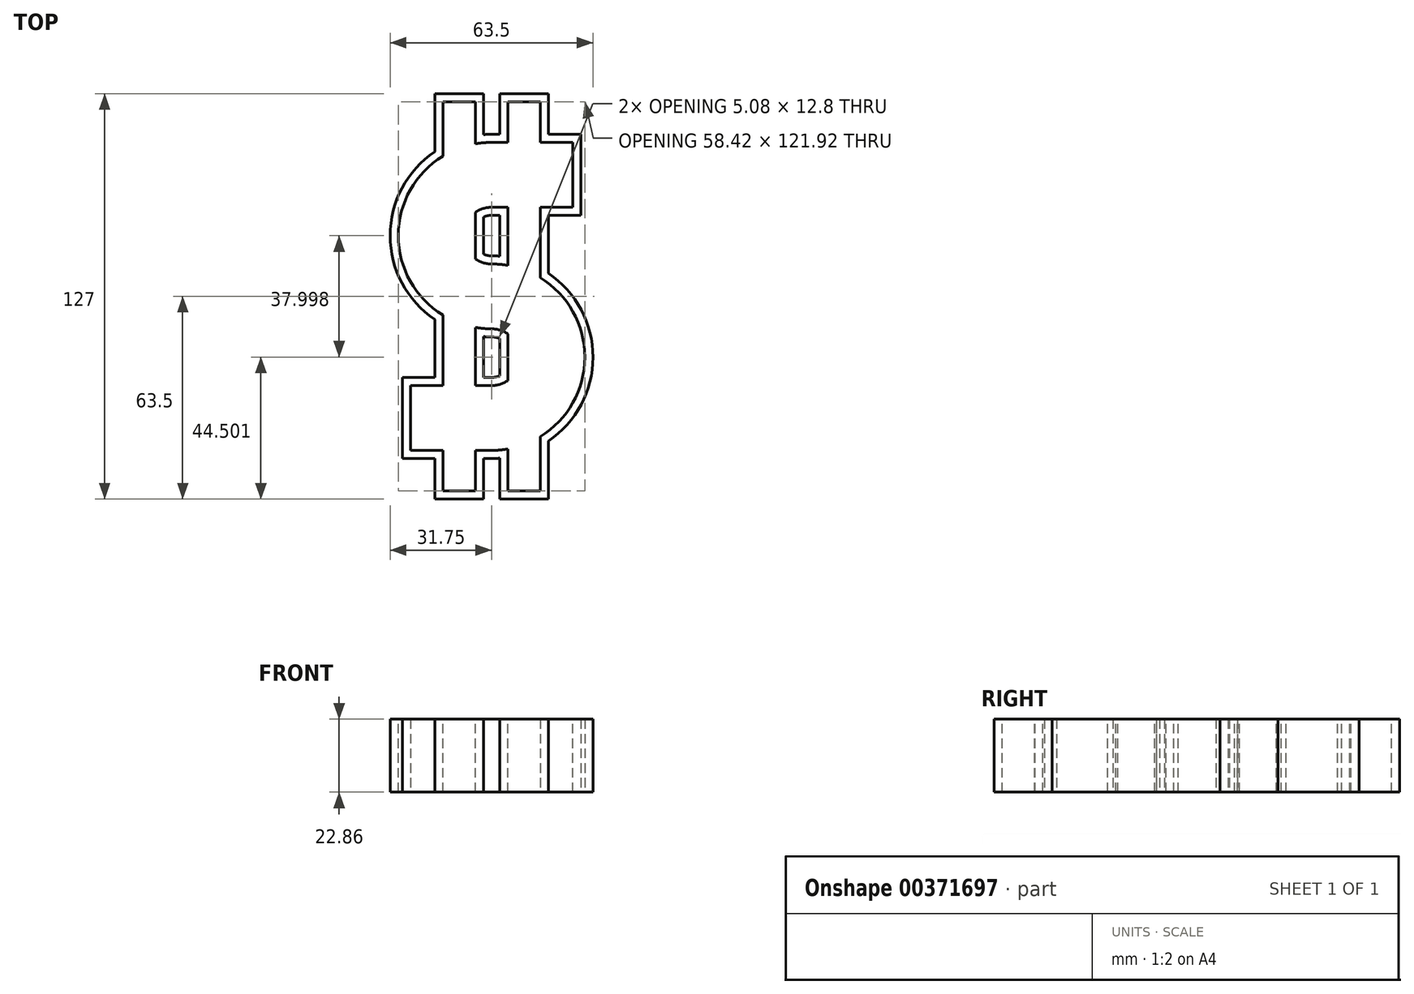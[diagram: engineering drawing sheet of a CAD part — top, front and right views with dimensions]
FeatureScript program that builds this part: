
annotation { "Feature Type Name" : "Feature", "Feature Type Description" : "" }
export const myFeature = defineFeature(function(context is Context, id is Id, definition is map)
    precondition{}
    {
        {
            var Q0;
            Q0=qCreatedBy(makeId("Top.planeOp"),FACE);
            var sketch = newSketch(context, id + "F0", { "sketchPlane" : qUnion([Q0])});
            skArc(sketch, "E0", {"start": v(0, 38.1) * mm, "mid": v(-19.05, 19.05) * mm, "end": v(0, 0) * mm});
            skArc(sketch, "E1", {"start": v(0, -38.1) * mm, "mid": v(19.05, -19.05) * mm, "end": v(0, 0) * mm});
            skLineSegment(sketch, "E2", {"start": v(-75.44, 0) * mm, "end": v(75.44, 0) * mm, "construction": true});
            skPoint(sketch, "E3", {"position": v(0, 38.1) * mm});
            skPoint(sketch, "E4", {"position": v(0, -38.1) * mm});
            skLineSegment(sketch, "E5", {"start": v(0, 38.1) * mm, "end": v(27.94, 38.1) * mm});
            skLineSegment(sketch, "E6", {"start": v(0, -38.1) * mm, "end": v(-27.94, -38.1) * mm});
            skSolve(sketch);
        }
        {
            var Q0;
            Q0=qCreatedBy(makeId("Right.planeOp"),FACE);
            cPlane(context, id + "F1", {"entities" : qUnion([Q0]), "cplaneType" : CPlaneType.OFFSET, "offset" : 27.94 * mm, "width" : 152.4 * mm, "height" : 152.4 * mm});
        }
        {
            var Q0;
            Q0=qCreatedBy(id+"F1.planeOp",FACE);
            var sketch = newSketch(context, id + "F2", { "sketchPlane" : qUnion([Q0])});
            skLineSegment(sketch, "E7.bottom", {"start": v(25.4, 12.7) * mm, "end": v(50.8, 12.7) * mm});
            skLineSegment(sketch, "E7.top", {"start": v(25.4, -12.7) * mm, "end": v(50.8, -12.7) * mm});
            skLineSegment(sketch, "E7.left", {"start": v(25.4, 12.7) * mm, "end": v(25.4, -12.7) * mm});
            skLineSegment(sketch, "E7.right", {"start": v(50.8, 12.7) * mm, "end": v(50.8, -12.7) * mm});
            skSolve(sketch);
        }
        {
            var Q0;
            Q0=makeQuery(id+"F2.imprint","IMPRINT",FACE,{"disambiguationData":[TD([[makeQuery(id+"F2.imprint","IMPRINT",EDGE,{"derivedFrom":sQuery(id+"F2.wireOp",EDGE,"E7.bottom")}),-1.0]])]});
            var Q1;
            Q1=sQuery(id+"F0.wireOp",EDGE,"E5");
            var Q2;
            Q2=sQuery(id+"F0.wireOp",EDGE,"E1");
            var Q3;
            Q3=sQuery(id+"F0.wireOp",EDGE,"E6");
            var Q4;
            Q4=sQuery(id+"F0.wireOp",EDGE,"E0");
            sweep(context, id + "F3", {"profiles" : qUnion([Q0]), "path" : qUnion([Q1, Q2, Q3, Q4])});
        }
        {
            var Q0;
            Q0=makeQuery(id+"F3.opSweep","SWEPT_FACE",FACE,{"disambiguationData":[OSD([sQuery(id+"F0.wireOp",EDGE,"E5"),sQuery(id+"F2.wireOp",EDGE,"E7.bottom")])]});
            var sketch = newSketch(context, id + "F4", { "sketchPlane" : qUnion([Q0])});
            skLineSegment(sketch, "E8.bottom", {"start": v(-17.78, 63.5) * mm, "end": v(-2.54, 63.5) * mm});
            skLineSegment(sketch, "E8.top", {"start": v(-17.78, -63.5) * mm, "end": v(-2.54, -63.5) * mm});
            skLineSegment(sketch, "E8.left", {"start": v(-17.78, 63.5) * mm, "end": v(-17.78, -63.5) * mm});
            skLineSegment(sketch, "E8.right", {"start": v(-2.54, 63.5) * mm, "end": v(-2.54, -63.5) * mm});
            skLineSegment(sketch, "E9.bottom", {"start": v(2.54, 63.5) * mm, "end": v(17.78, 63.5) * mm});
            skLineSegment(sketch, "E9.top", {"start": v(2.54, -63.5) * mm, "end": v(17.78, -63.5) * mm});
            skLineSegment(sketch, "E9.left", {"start": v(2.54, 63.5) * mm, "end": v(2.54, -63.5) * mm});
            skLineSegment(sketch, "E9.right", {"start": v(17.78, 63.5) * mm, "end": v(17.78, -63.5) * mm});
            skSolve(sketch);
        }
        {
            var Q0;
            {var subQ0=sQuery(id+"F4.wireOp",EDGE,"E8.bottom");Q0=makeQuery(id+"F4.imprint","IMPRINT",FACE,{"disambiguationData":[TD([[makeQuery(id+"F4.imprint","IMPRINT",EDGE,{"derivedFrom":subQ0}),-1.0]])]});}
            var Q1;
            {var subQ0=sQuery(id+"F4.wireOp",EDGE,"E9.bottom");Q1=makeQuery(id+"F4.imprint","IMPRINT",FACE,{"disambiguationData":[TD([[makeQuery(id+"F4.imprint","IMPRINT",EDGE,{"derivedFrom":subQ0}),-1.0]])]});}
            var Q2;
            {var subQ0=sQuery(id+"F4.wireOp",EDGE,"E8.top");Q2=makeQuery(id+"F4.imprint","IMPRINT",FACE,{"disambiguationData":[TD([[makeQuery(id+"F4.imprint","IMPRINT",EDGE,{"derivedFrom":subQ0}),1.0]])]});}
            var Q3;
            {var subQ0=sQuery(id+"F4.wireOp",EDGE,"E9.top");Q3=makeQuery(id+"F4.imprint","IMPRINT",FACE,{"disambiguationData":[TD([[makeQuery(id+"F4.imprint","IMPRINT",EDGE,{"derivedFrom":subQ0}),1.0]])]});}
            var Q4;
            {var subQ0=sQuery(id+"F4.wireOp",EDGE,"E8.left");var subQ1=sQuery(id+"F2.wireOp",EDGE,"E7.right");var subQ2=sQuery(id+"F2.wireOp",EDGE,"E7.bottom");var subQ3=makeQuery(id+"F3.opSweep","SWEPT_EDGE",EDGE,{"disambiguationData":[OSD([sQuery(id+"F0.wireOp",EDGE,"E0"),subQ2,subQ1])]});var subQ4=makeQuery(id+"F4.imprint","INTERSECT",VERTEX,{"disambiguationData":[OD(1.0)],"derivedFrom":[subQ3,subQ0]});Q4=makeQuery(id+"F4.imprint","IMPRINT",FACE,{"disambiguationData":[TD([[makeQuery(id+"F4.imprint","IMPRINT",EDGE,{"disambiguationData":[TD([[subQ4,-1.0]])],"derivedFrom":subQ0}),1.0]])]});}
            var Q5;
            {var subQ0=sQuery(id+"F4.wireOp",EDGE,"E9.left");var subQ1=sQuery(id+"F2.wireOp",EDGE,"E7.left");var subQ2=sQuery(id+"F2.wireOp",EDGE,"E7.bottom");var subQ3=makeQuery(id+"F3.opSweep","SWEPT_EDGE",EDGE,{"disambiguationData":[OSD([sQuery(id+"F0.wireOp",EDGE,"E5"),subQ2,subQ1])]});var subQ4=makeQuery(id+"F4.imprint","INTERSECT",VERTEX,{"derivedFrom":[subQ3,subQ0]});Q5=makeQuery(id+"F4.imprint","IMPRINT",FACE,{"disambiguationData":[TD([[makeQuery(id+"F4.imprint","IMPRINT",EDGE,{"disambiguationData":[TD([[subQ4,-1.0]])],"derivedFrom":subQ0}),1.0]])]});}
            var Q6;
            {var subQ0=sQuery(id+"F4.wireOp",EDGE,"E9.left");var subQ1=makeQuery(id+"F3.opSweep","SWEPT_EDGE",EDGE,{"disambiguationData":[OSD([sQuery(id+"F0.wireOp",EDGE,"E1"),sQuery(id+"F2.wireOp",EDGE,"E7.bottom"),sQuery(id+"F2.wireOp",EDGE,"E7.right")])]});var subQ2=makeQuery(id+"F4.imprint","INTERSECT",VERTEX,{"disambiguationData":[OD(0.0)],"derivedFrom":[subQ1,subQ0]});Q6=makeQuery(id+"F4.imprint","IMPRINT",FACE,{"disambiguationData":[TD([[makeQuery(id+"F4.imprint","IMPRINT",EDGE,{"disambiguationData":[TD([[subQ2,-1.0]])],"derivedFrom":subQ0}),1.0]])]});}
            var Q7;
            {var subQ0=sQuery(id+"F4.wireOp",EDGE,"E8.right");var subQ1=makeQuery(id+"F3.opSweep","SWEPT_EDGE",EDGE,{"disambiguationData":[OSD([sQuery(id+"F0.wireOp",EDGE,"E0"),sQuery(id+"F2.wireOp",EDGE,"E7.bottom"),sQuery(id+"F2.wireOp",EDGE,"E7.left")])]});var subQ2=makeQuery(id+"F4.imprint","INTERSECT",VERTEX,{"disambiguationData":[OD(0.0)],"derivedFrom":[subQ1,subQ0]});Q7=makeQuery(id+"F4.imprint","IMPRINT",FACE,{"disambiguationData":[TD([[makeQuery(id+"F4.imprint","IMPRINT",EDGE,{"disambiguationData":[TD([[subQ2,-1.0]])],"derivedFrom":subQ0}),-1.0]])]});}
            extrude(context, id + "F5", {"entities" : qUnion([Q0, Q1, Q2, Q3, Q4, Q5, Q6, Q7]), "operationType" : NewBodyOperationType.ADD, "oppositeDirection" : true, "depth" : 25.4 * mm});
        }
        {
            var Q0;
            {var subQ0=sQuery(id+"F4.wireOp",EDGE,"E9.right");var subQ1=sQuery(id+"F4.wireOp",EDGE,"E9.left");var subQ2=sQuery(id+"F2.wireOp",EDGE,"E7.left");var subQ3=sQuery(id+"F2.wireOp",EDGE,"E7.bottom");var subQ4=sQuery(id+"F2.wireOp",EDGE,"E7.right");var subQ5=sQuery(id+"F0.wireOp",EDGE,"E5");var subQ6=sQuery(id+"F4.wireOp",EDGE,"E8.right");var subQ7=sQuery(id+"F4.wireOp",EDGE,"E8.left");Q0=makeQuery(id+"F5.boolean.opBoolean","MERGE",FACE,{"derivedFrom":[makeQuery(id+"F3.opSweep","SWEPT_FACE",FACE,{"disambiguationData":[OSD([subQ5,subQ3])]}),makeQuery(id+"F5.opExtrude","CAP_FACE",FACE,{"disambiguationData":[OSD([sQuery(id+"F0.wireOp",EDGE,"E0"),subQ3,subQ4,sQuery(id+"F4.wireOp",EDGE,"E8.bottom"),subQ7,subQ6])],"isStart":true}),makeQuery(id+"F5.opExtrude","CAP_FACE",FACE,{"disambiguationData":[OSD([sQuery(id+"F0.wireOp",EDGE,"E6"),subQ3,subQ2,sQuery(id+"F4.wireOp",EDGE,"E8.top"),subQ7,subQ6])],"isStart":true}),makeQuery(id+"F5.opExtrude","CAP_FACE",FACE,{"disambiguationData":[OSD([subQ5,subQ3,subQ4,sQuery(id+"F4.wireOp",EDGE,"E9.bottom"),subQ1,subQ0])],"isStart":true}),makeQuery(id+"F5.opExtrude","CAP_FACE",FACE,{"disambiguationData":[OSD([sQuery(id+"F0.wireOp",EDGE,"E1"),subQ3,subQ2,sQuery(id+"F4.wireOp",EDGE,"E9.top"),subQ1,subQ0])],"isStart":true})]});}
            shell(context, id + "F6", {"entities" : qUnion([Q0]), "thickness" : 2.54 * mm});
        }
        {
            var Q0;
            {var subQ0=sQuery(id+"F4.wireOp",EDGE,"E9.right");var subQ1=sQuery(id+"F4.wireOp",EDGE,"E9.left");var subQ2=sQuery(id+"F2.wireOp",EDGE,"E7.left");var subQ3=sQuery(id+"F2.wireOp",EDGE,"E7.bottom");var subQ4=sQuery(id+"F2.wireOp",EDGE,"E7.right");var subQ5=sQuery(id+"F0.wireOp",EDGE,"E5");var subQ6=sQuery(id+"F4.wireOp",EDGE,"E8.right");var subQ7=sQuery(id+"F4.wireOp",EDGE,"E8.left");Q0=makeQuery(id+"F5.boolean.opBoolean","MERGE",FACE,{"derivedFrom":[makeQuery(id+"F3.opSweep","SWEPT_FACE",FACE,{"disambiguationData":[OSD([subQ5,sQuery(id+"F2.wireOp",EDGE,"E7.top")])]}),makeQuery(id+"F5.opExtrude","CAP_FACE",FACE,{"disambiguationData":[OSD([sQuery(id+"F0.wireOp",EDGE,"E0"),subQ3,subQ4,sQuery(id+"F4.wireOp",EDGE,"E8.bottom"),subQ7,subQ6])],"isStart":false}),makeQuery(id+"F5.opExtrude","CAP_FACE",FACE,{"disambiguationData":[OSD([sQuery(id+"F0.wireOp",EDGE,"E6"),subQ3,subQ2,sQuery(id+"F4.wireOp",EDGE,"E8.top"),subQ7,subQ6])],"isStart":false}),makeQuery(id+"F5.opExtrude","CAP_FACE",FACE,{"disambiguationData":[OSD([subQ5,subQ3,subQ4,sQuery(id+"F4.wireOp",EDGE,"E9.bottom"),subQ1,subQ0])],"isStart":false}),makeQuery(id+"F5.opExtrude","CAP_FACE",FACE,{"disambiguationData":[OSD([sQuery(id+"F0.wireOp",EDGE,"E1"),subQ3,subQ2,sQuery(id+"F4.wireOp",EDGE,"E9.top"),subQ1,subQ0])],"isStart":false})]});}
            extrude(context, id + "F7", {"entities" : qUnion([Q0]), "operationType" : NewBodyOperationType.REMOVE, "oppositeDirection" : true, "depth" : 2.54 * mm});
        }
    });
